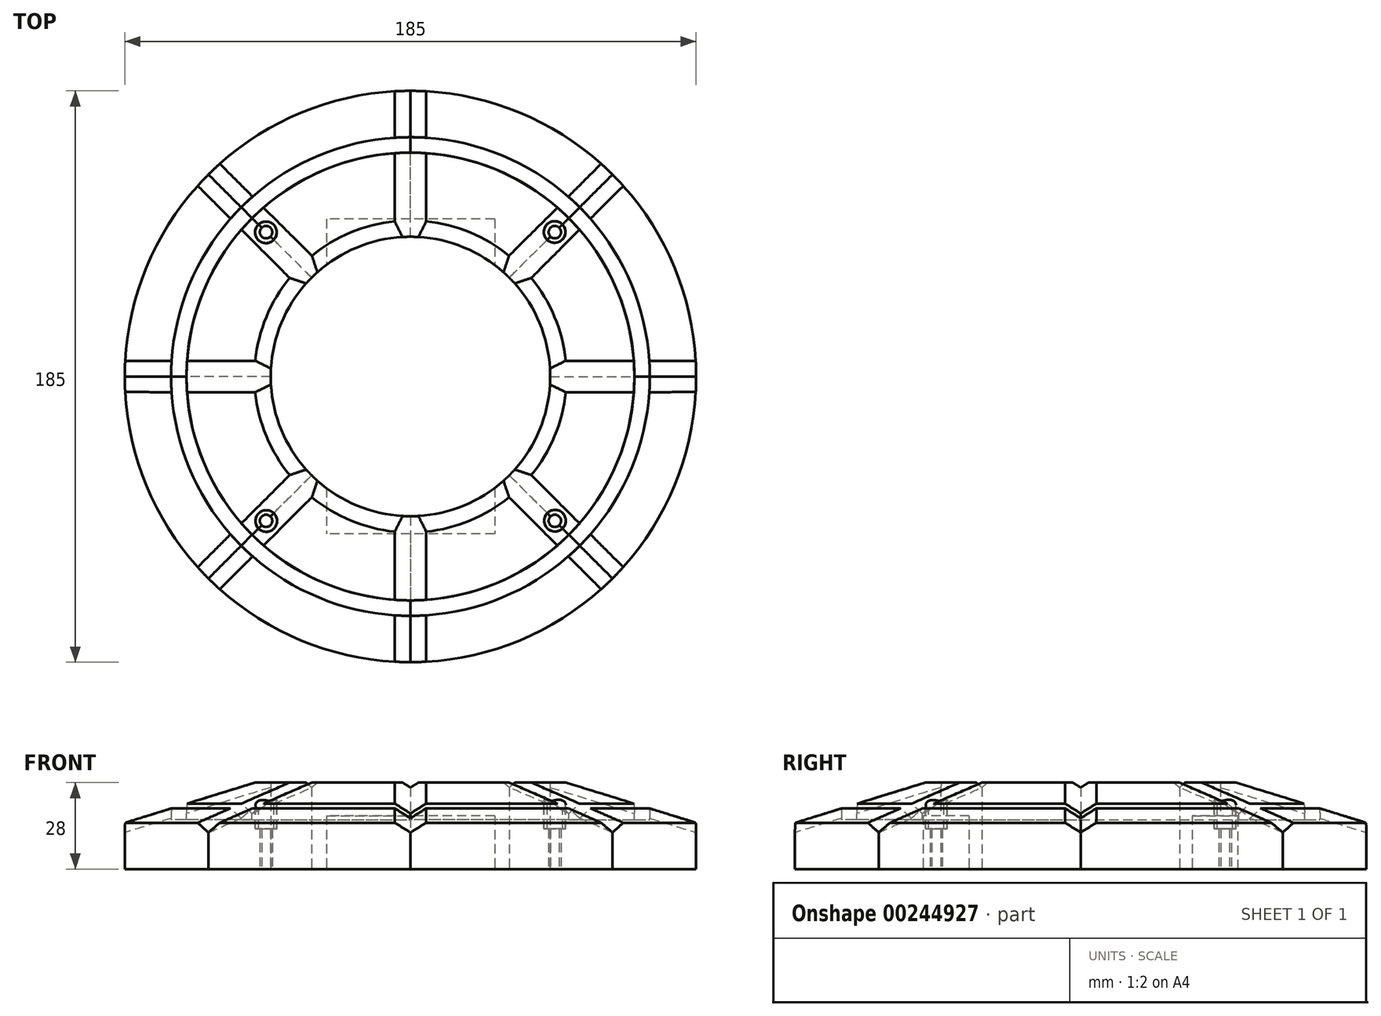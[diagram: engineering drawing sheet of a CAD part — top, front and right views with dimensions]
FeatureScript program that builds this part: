
annotation { "Feature Type Name" : "Feature", "Feature Type Description" : "" }
export const myFeature = defineFeature(function(context is Context, id is Id, definition is map)
    precondition{}
    {
        {
            var Q0;
            Q0=qCreatedBy(makeId("Top.planeOp"),FACE);
            var sketch = newSketch(context, id + "F0", { "sketchPlane" : qUnion([Q0])});
            skArc(sketch, "E0", {"start": v(92.5, 0) * mm, "mid": v(85.46, 35.4) * mm, "end": v(65.4, 65.4) * mm});
            skArc(sketch, "E1", {"start": v(45.25, 0) * mm, "mid": v(41.8, 17.32) * mm, "end": v(32, 32) * mm});
            skLineSegment(sketch, "E2", {"start": v(45.25, 0) * mm, "end": v(92.5, 0) * mm});
            skLineSegment(sketch, "E3", {"start": v(32, 32) * mm, "end": v(65.4, 65.4) * mm});
            skSolve(sketch);
        }
        {
            var Q0;
            Q0 = qSketchRegion(id + "F0", true);
            extrude(context, id + "F1", {"entities" : qUnion([Q0]), "depth" : 28 * mm});
        }
        {
            var Q0;
            Q0=makeQuery(id+"F1.opExtrude","CAP_EDGE",EDGE,{"disambiguationData":[OSD([sQuery(id+"F0.wireOp",EDGE,"E0")])],"isStart":false});
            chamfer(context, id + "F2", {"entities" : qUnion([Q0]), "chamferType" : ChamferType.TWO_OFFSETS, "width1" : 42 * mm, "oppositeDirection" : false, "width2" : 13 * mm, "tangentPropagation" : true});
        }
        {
            var Q0;
            Q0=makeQuery(id+"F2.opChamfer","BLEND_EDGE",EDGE,{"blendedFrom":[makeQuery(id+"F1.opExtrude","CAP_EDGE",EDGE,{"disambiguationData":[OSD([sQuery(id+"F0.wireOp",EDGE,"E0")])],"isStart":false}),makeQuery(id+"F1.opExtrude","SWEPT_FACE",FACE,{"disambiguationData":[OSD([sQuery(id+"F0.wireOp",EDGE,"E2")])]})],"blendedInto":[makeQuery(id+"F1.opExtrude","SWEPT_FACE",FACE,{"disambiguationData":[OSD([sQuery(id+"F0.wireOp",EDGE,"E2")])]})]});
            var Q1;
            Q1=makeQuery(id+"F2.opChamfer","BLEND_EDGE",EDGE,{"blendedFrom":[makeQuery(id+"F1.opExtrude","CAP_EDGE",EDGE,{"disambiguationData":[OSD([sQuery(id+"F0.wireOp",EDGE,"E0")])],"isStart":false}),makeQuery(id+"F1.opExtrude","SWEPT_FACE",FACE,{"disambiguationData":[OSD([sQuery(id+"F0.wireOp",EDGE,"E3")])]})],"blendedInto":[makeQuery(id+"F1.opExtrude","SWEPT_FACE",FACE,{"disambiguationData":[OSD([sQuery(id+"F0.wireOp",EDGE,"E3")])]})]});
            chamfer(context, id + "F3", {"entities" : qUnion([Q0, Q1]), "chamferType" : ChamferType.TWO_OFFSETS, "width1" : 3 * mm, "oppositeDirection" : false, "width2" : 5 * mm, "tangentPropagation" : true});
        }
        {
            var Q0;
            Q0=makeQuery(id+"F1.opExtrude","SWEPT_BODY",BODY,{"disambiguationData":[OSD([sQuery(id+"F0.wireOp",EDGE,"E0"),sQuery(id+"F0.wireOp",EDGE,"E1"),sQuery(id+"F0.wireOp",EDGE,"E2"),sQuery(id+"F0.wireOp",EDGE,"E3")])]});
            var Q1;
            Q1=makeQuery(id+"F1.opExtrude","SWEPT_FACE",FACE,{"disambiguationData":[OSD([sQuery(id+"F0.wireOp",EDGE,"E1")])]});
            circularPattern(context, id + "F4", {"entities" : qUnion([Q0]), "axis" : qUnion([Q1]), "angle" : 360 * degree, "instanceCount" : 8, "equalSpace" : true});
        }
        {
            var Q0;
            Q0=qCreatedBy(makeId("Top.planeOp"),FACE);
            var sketch = newSketch(context, id + "F5", { "sketchPlane" : qUnion([Q0])});
            skLineSegment(sketch, "E4", {"start": v(64.43, 64.43) * mm, "end": v(46.75, 46.75) * mm});
            skCircle(sketch, "E5", {"center": v(46.75, 46.75) * mm, "radius": 2 * mm});
            skCircle(sketch, "E6.1.0", {"center": v(46.75, -46.75) * mm, "radius": 2 * mm});
            skCircle(sketch, "E6.2.0", {"center": v(-46.75, -46.75) * mm, "radius": 2 * mm});
            skCircle(sketch, "E6.3.0", {"center": v(-46.75, 46.75) * mm, "radius": 2 * mm});
            skPoint(sketch, "E6.center", {"position": v(0, 0) * mm});
            skLineSegment(sketch, "E6.anchor1", {"start": v(0, 0) * mm, "end": v(46.75, 46.75) * mm, "construction": true});
            skLineSegment(sketch, "E6.anchor2", {"start": v(0, 0) * mm, "end": v(-46.75, 46.75) * mm, "construction": true});
            skLineSegment(sketch, "E7", {"start": v(-46.75, 46.75) * mm, "end": v(46.75, 46.75) * mm});
            skSolve(sketch);
        }
        {
            var Q0;
            Q0 = qSketchRegion(id + "F5", true);
            extrude(context, id + "F6", {"entities" : qUnion([Q0]), "operationType" : NewBodyOperationType.REMOVE, "depth" : 25 * mm});
        }
        {
            var Q0;
            Q0=makeQuery(id+"F4.opPattern","COPY",FACE,{"derivedFrom":makeQuery(id+"F1.opExtrude","CAP_FACE",FACE,{"disambiguationData":[OSD([sQuery(id+"F0.wireOp",EDGE,"E0"),sQuery(id+"F0.wireOp",EDGE,"E1"),sQuery(id+"F0.wireOp",EDGE,"E2"),sQuery(id+"F0.wireOp",EDGE,"E3")])],"isStart":false}),"instanceName":"3"});
            var sketch = newSketch(context, id + "F7", { "sketchPlane" : qUnion([Q0])});
            skCircle(sketch, "E8", {"center": v(0, 0) * mm, "radius": 77.5 * mm});
            skCircle(sketch, "E9", {"center": v(0, 0) * mm, "radius": 72.5 * mm});
            skSolve(sketch);
        }
        {
            var Q0;
            Q0 = qSketchRegion(id + "F7", true);
            extrude(context, id + "F8", {"entities" : qUnion([Q0]), "operationType" : NewBodyOperationType.REMOVE, "oppositeDirection" : true, "depth" : 12 * mm});
        }
        {
            var Q0;
            Q0=makeQuery(id+"F4.opPattern","COPY",FACE,{"derivedFrom":makeQuery(id+"F1.opExtrude","CAP_FACE",FACE,{"disambiguationData":[OSD([sQuery(id+"F0.wireOp",EDGE,"E0"),sQuery(id+"F0.wireOp",EDGE,"E1"),sQuery(id+"F0.wireOp",EDGE,"E2"),sQuery(id+"F0.wireOp",EDGE,"E3")])],"isStart":false}),"instanceName":"3"});
            var sketch = newSketch(context, id + "F9", { "sketchPlane" : qUnion([Q0])});
            skLineSegment(sketch, "E10", {"start": v(0, 0) * mm, "end": v(46.68, 46.8) * mm});
            skCircle(sketch, "E11", {"center": v(46.68, 46.8) * mm, "radius": 3.5 * mm});
            skCircle(sketch, "E12.1.0", {"center": v(-46.8, 46.68) * mm, "radius": 3.5 * mm});
            skCircle(sketch, "E12.2.0", {"center": v(-46.68, -46.8) * mm, "radius": 3.5 * mm});
            skCircle(sketch, "E12.3.0", {"center": v(46.8, -46.68) * mm, "radius": 3.5 * mm});
            skPoint(sketch, "E12.center", {"position": v(0, 0) * mm});
            skSolve(sketch);
        }
        {
            var Q0;
            {Q0=qUnion([makeQuery(id+"F9.imprint","IMPRINT",FACE,{"disambiguationData":[TD([[makeQuery(id+"F9.imprint","IMPRINT",EDGE,{"derivedFrom":sQuery(id+"F9.wireOp",EDGE,"E11")}),1.0]])]}),makeQuery(id+"F9.imprint","IMPRINT",FACE,{"disambiguationData":[TD([[makeQuery(id+"F9.imprint","IMPRINT",EDGE,{"derivedFrom":sQuery(id+"F9.wireOp",EDGE,"E12.1.0")}),1.0]])]}),makeQuery(id+"F9.imprint","IMPRINT",FACE,{"disambiguationData":[TD([[makeQuery(id+"F9.imprint","IMPRINT",EDGE,{"derivedFrom":sQuery(id+"F9.wireOp",EDGE,"E12.2.0")}),1.0]])]}),makeQuery(id+"F9.imprint","IMPRINT",FACE,{"disambiguationData":[TD([[makeQuery(id+"F9.imprint","IMPRINT",EDGE,{"derivedFrom":sQuery(id+"F9.wireOp",EDGE,"E12.3.0")}),1.0]])]})]);}
            extrude(context, id + "F10", {"entities" : qUnion([Q0]), "operationType" : NewBodyOperationType.REMOVE, "oppositeDirection" : true, "depth" : 15 * mm});
        }
        {
            var Q0;
            Q0=qCreatedBy(makeId("Top.planeOp"),FACE);
            var sketch = newSketch(context, id + "F11", { "sketchPlane" : qUnion([Q0])});
            skLineSegment(sketch, "E13.bottom", {"start": v(27.25, 51) * mm, "end": v(-27.25, 51) * mm});
            skLineSegment(sketch, "E13.top", {"start": v(27.25, -51) * mm, "end": v(-27.25, -51) * mm});
            skLineSegment(sketch, "E13.left", {"start": v(27.25, 51) * mm, "end": v(27.25, -51) * mm});
            skLineSegment(sketch, "E13.right", {"start": v(-27.25, 51) * mm, "end": v(-27.25, -51) * mm});
            skPoint(sketch, "E13.middle", {"position": v(0, 0) * mm});
            skSolve(sketch);
        }
        {
            var Q0;
            Q0 = qSketchRegion(id + "F11", true);
            extrude(context, id + "F12", {"entities" : qUnion([Q0]), "operationType" : NewBodyOperationType.REMOVE, "depth" : 17.25 * mm});
        }
    });
